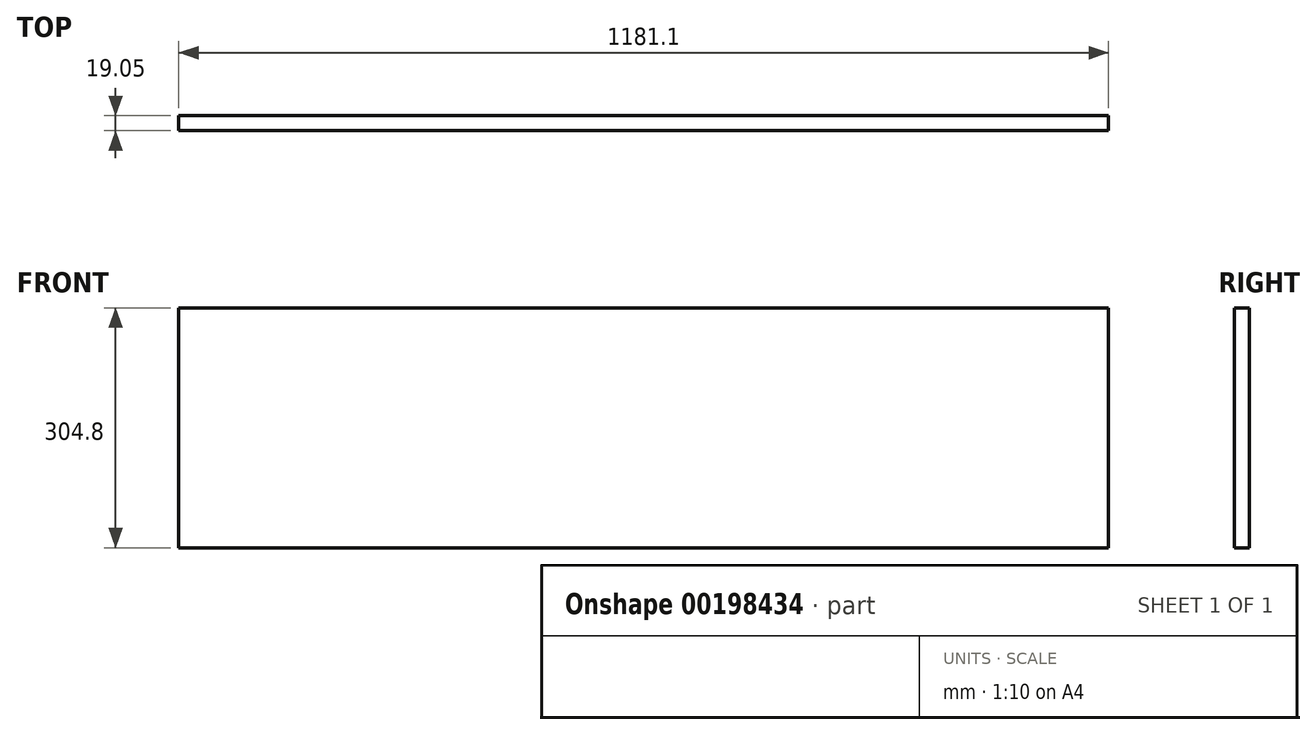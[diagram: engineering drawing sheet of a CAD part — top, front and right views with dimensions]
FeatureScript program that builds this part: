
annotation { "Feature Type Name" : "Feature", "Feature Type Description" : "" }
export const myFeature = defineFeature(function(context is Context, id is Id, definition is map)
    precondition{}
    {
        {
            var Q0;
            Q0=qCreatedBy(makeId("Front.planeOp"),FACE);
            var sketch = newSketch(context, id + "F0", { "sketchPlane" : qUnion([Q0])});
            skLineSegment(sketch, "E0.bottom", {"start": v(0, 0) * mm, "end": v(1181.1, 0) * mm});
            skLineSegment(sketch, "E0.top", {"start": v(0, 304.8) * mm, "end": v(1181.1, 304.8) * mm});
            skLineSegment(sketch, "E0.left", {"start": v(0, 0) * mm, "end": v(0, 304.8) * mm});
            skLineSegment(sketch, "E0.right", {"start": v(1181.1, 0) * mm, "end": v(1181.1, 304.8) * mm});
            skSolve(sketch);
        }
        {
            var Q0;
            Q0 = qSketchRegion(id + "F0", true);
            extrude(context, id + "F1", {"entities" : qUnion([Q0]), "depth" : 19.05 * mm});
        }
    });
